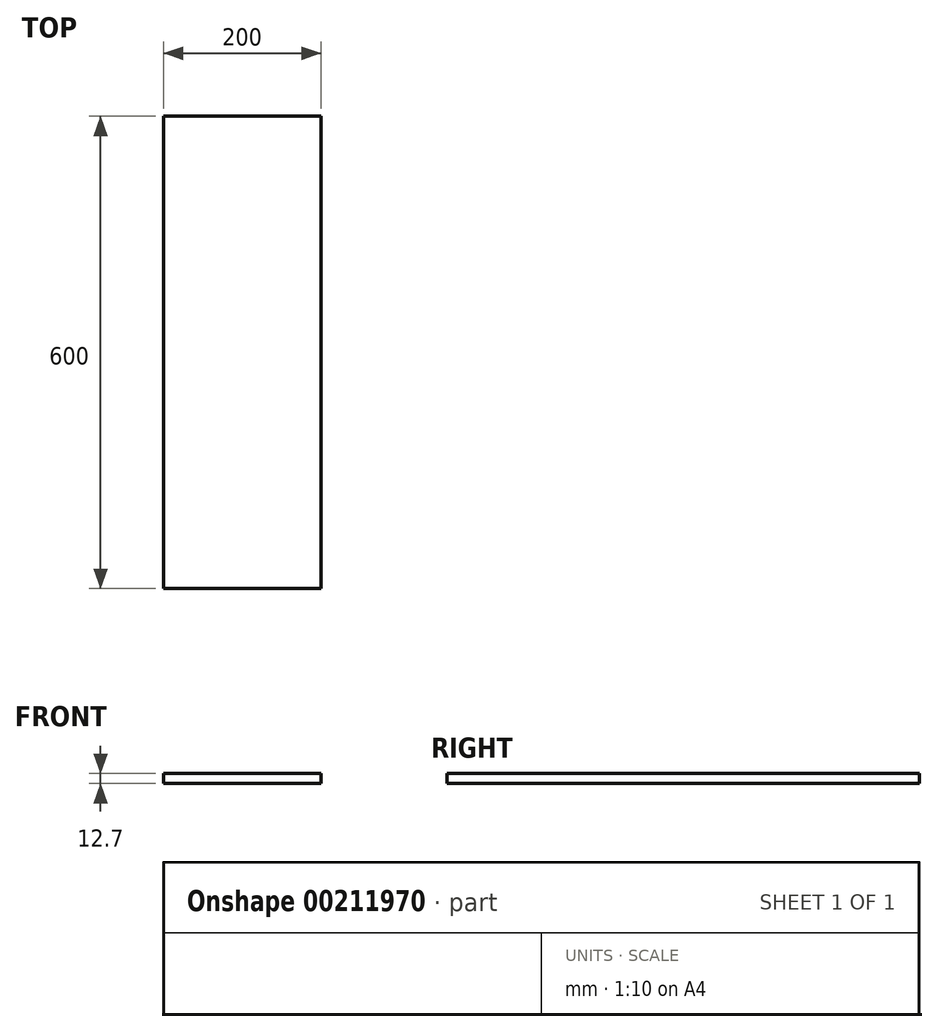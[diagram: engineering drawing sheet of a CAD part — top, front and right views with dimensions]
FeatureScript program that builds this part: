
annotation { "Feature Type Name" : "Feature", "Feature Type Description" : "" }
export const myFeature = defineFeature(function(context is Context, id is Id, definition is map)
    precondition{}
    {
        {
            var Q0;
            Q0=qCreatedBy(makeId("Top.planeOp"),FACE);
            var sketch = newSketch(context, id + "F0", { "sketchPlane" : qUnion([Q0])});
            skLineSegment(sketch, "E0.bottom", {"start": v(100, -300) * mm, "end": v(-100, -300) * mm});
            skLineSegment(sketch, "E0.top", {"start": v(100, 300) * mm, "end": v(-100, 300) * mm});
            skLineSegment(sketch, "E0.left", {"start": v(100, -300) * mm, "end": v(100, 300) * mm});
            skLineSegment(sketch, "E0.right", {"start": v(-100, -300) * mm, "end": v(-100, 300) * mm});
            skPoint(sketch, "E0.middle", {"position": v(0, 0) * mm});
            skSolve(sketch);
        }
        {
            var Q0;
            Q0=makeQuery(id+"F0.imprint","IMPRINT",FACE,{"disambiguationData":[TD([[makeQuery(id+"F0.imprint","IMPRINT",EDGE,{"derivedFrom":sQuery(id+"F0.wireOp",EDGE,"E0.bottom")}),-1.0]])]});
            extrude(context, id + "F1", {"entities" : qUnion([Q0]), "depth" : 12.7 * mm});
        }
    });
